# Revit family: P1001_3_Column
name_source: partatom
category: Structural Columns
units: mm (PartAtom-declared; Revit-internal decimal feet)

## family parameters
Always export as geometry = No
Beam cutback in plan = From bounding box
Cut with Voids When Loaded = No
Material for Model Behavior = Other
OmniClass Number = 23.25.30.11.14.11
OmniClass Title = Columns
Section Shape = Not Defined
Shared = Yes
Show family pre-cut in plan views = Yes

## types (5) — shared parameters
Assembly Code = B10
Description = P1001-3 - Column - 1-5/8" x 4 7/8", 12 Gauge, Triple Combination
Height = 4.875 "
Manufacturer = Atkore Unistrut
Model = P1001-3
Salsify ID1 = US-P1001-3
URL = https://www.atkore.com

## per-type parameters (varying)
| type | Structural Material | UPC-10ft | UPC-20ft | Unit Weight |
| P1001-3 PL | Plain | "786364014210" | "786364014258" | 5.66 lb/ft |
| P1001-3 HG | Hot Dip Galvanized | "786364014197" | "786364014234" | 5.7 lb/ft |
| P1001-3 GR | Green |  | "786364014227" | 5.7 lb/ft |
| P1001-3 PG | Pre-Galvanized | "786364014203" | "786364014241" | 5.66 lb/ft |
| P1001-3 SS | Stainless Steel |  | "0" | 5.7 lb/ft |

note: column(s) folded — value = type name in every type: Part Number

## geometry (parser evidence)
native form markers: Sweep x6
no freeform markers — native parametric forms only
